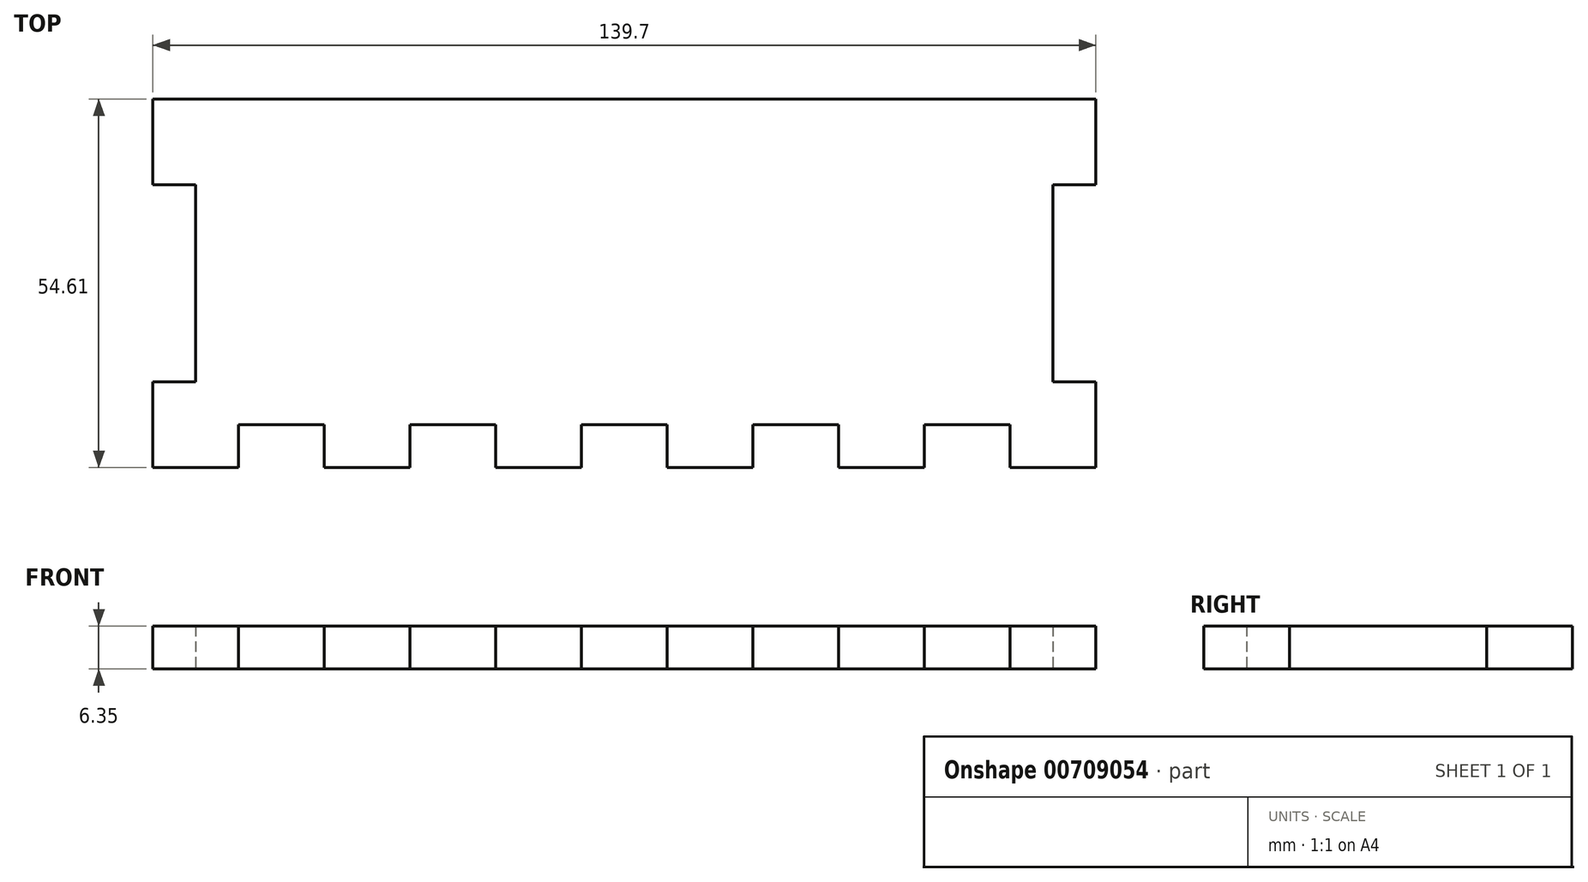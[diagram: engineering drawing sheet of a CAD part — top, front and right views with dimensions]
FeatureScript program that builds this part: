
annotation { "Feature Type Name" : "Feature", "Feature Type Description" : "" }
export const myFeature = defineFeature(function(context is Context, id is Id, definition is map)
    precondition{}
    {
        {
            var Q0;
            Q0=qCreatedBy(makeId("Top.planeOp"),FACE);
            var sketch = newSketch(context, id + "F0", { "sketchPlane" : qUnion([Q0])});
            skLineSegment(sketch, "E0.bottom", {"start": v(0, 0) * mm, "end": v(139.7, 0) * mm});
            skLineSegment(sketch, "E0.top", {"start": v(0, -54.6) * mm, "end": v(12.7, -54.6) * mm});
            skLineSegment(sketch, "E0.left", {"start": v(0, 0) * mm, "end": v(0, -12.7) * mm});
            skLineSegment(sketch, "E1", {"start": v(12.7, -54.6) * mm, "end": v(12.7, -48.26) * mm});
            skLineSegment(sketch, "E2", {"start": v(12.7, -48.26) * mm, "end": v(25.4, -48.26) * mm});
            skLineSegment(sketch, "E3", {"start": v(25.4, -48.26) * mm, "end": v(25.4, -54.6) * mm});
            skLineSegment(sketch, "E4", {"start": v(25.4, -54.6) * mm, "end": v(38.1, -54.6) * mm});
            skLineSegment(sketch, "E5", {"start": v(38.1, -54.61) * mm, "end": v(38.1, -48.26) * mm});
            skLineSegment(sketch, "E6", {"start": v(38.1, -48.26) * mm, "end": v(50.8, -48.26) * mm});
            skLineSegment(sketch, "E7", {"start": v(50.8, -48.26) * mm, "end": v(50.8, -54.6) * mm});
            skLineSegment(sketch, "E8", {"start": v(50.8, -54.6) * mm, "end": v(63.5, -54.6) * mm});
            skLineSegment(sketch, "E9", {"start": v(63.5, -54.61) * mm, "end": v(63.5, -48.26) * mm});
            skLineSegment(sketch, "E10", {"start": v(63.5, -48.26) * mm, "end": v(76.2, -48.26) * mm});
            skLineSegment(sketch, "E11", {"start": v(76.2, -48.26) * mm, "end": v(76.2, -54.61) * mm});
            skLineSegment(sketch, "E12", {"start": v(76.2, -54.6) * mm, "end": v(88.9, -54.6) * mm});
            skLineSegment(sketch, "E13", {"start": v(88.9, -54.6) * mm, "end": v(88.9, -48.26) * mm});
            skLineSegment(sketch, "E14", {"start": v(88.9, -48.26) * mm, "end": v(101.6, -48.26) * mm});
            skLineSegment(sketch, "E15", {"start": v(101.6, -48.26) * mm, "end": v(101.6, -54.61) * mm});
            skLineSegment(sketch, "E16.trimOffspring", {"start": v(101.6, -54.6) * mm, "end": v(114.3, -54.6) * mm});
            skLineSegment(sketch, "E17", {"start": v(114.3, -54.61) * mm, "end": v(114.3, -48.26) * mm});
            skLineSegment(sketch, "E18", {"start": v(114.3, -48.26) * mm, "end": v(127, -48.26) * mm});
            skLineSegment(sketch, "E19", {"start": v(127, -48.26) * mm, "end": v(127, -54.61) * mm});
            skLineSegment(sketch, "E20.trimOffspring", {"start": v(127, -54.6) * mm, "end": v(139.7, -54.6) * mm});
            skLineSegment(sketch, "E21", {"start": v(0, -54.61) * mm, "end": v(0, -41.91) * mm});
            skLineSegment(sketch, "E22", {"start": v(0, -41.91) * mm, "end": v(6.35, -41.91) * mm});
            skLineSegment(sketch, "E23", {"start": v(6.35, -41.91) * mm, "end": v(6.35, -12.7) * mm});
            skLineSegment(sketch, "E24", {"start": v(6.35, -12.7) * mm, "end": v(0, -12.7) * mm});
            skLineSegment(sketch, "E25.trimOffspring", {"start": v(0, -41.91) * mm, "end": v(0, -54.61) * mm});
            skLineSegment(sketch, "E26", {"start": v(69.85, -48.26) * mm, "end": v(69.85, -22.86) * mm, "construction": true});
            skLineSegment(sketch, "E27.MirrorCS", {"start": v(139.7, 0) * mm, "end": v(139.7, -12.7) * mm});
            skLineSegment(sketch, "E28.MirrorCS", {"start": v(133.35, -12.7) * mm, "end": v(139.7, -12.7) * mm});
            skLineSegment(sketch, "E29.MirrorCS", {"start": v(133.35, -41.91) * mm, "end": v(133.35, -12.7) * mm});
            skLineSegment(sketch, "E30.MirrorCS", {"start": v(139.7, -41.91) * mm, "end": v(133.35, -41.91) * mm});
            skLineSegment(sketch, "E31.MirrorCS", {"start": v(139.7, -41.91) * mm, "end": v(139.7, -54.61) * mm});
            skSolve(sketch);
        }
        {
            var Q0;
            Q0=makeQuery(id+"F0.imprint","IMPRINT",FACE,{"disambiguationData":[TD([[makeQuery(id+"F0.imprint","IMPRINT",EDGE,{"derivedFrom":sQuery(id+"F0.wireOp",EDGE,"E0.bottom")}),-1.0]])]});
            extrude(context, id + "F1", {"entities" : qUnion([Q0]), "depth" : 6.35 * mm, "offsetDistance" : 25.4 * mm});
        }
    });
